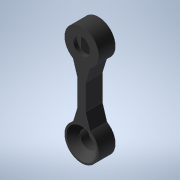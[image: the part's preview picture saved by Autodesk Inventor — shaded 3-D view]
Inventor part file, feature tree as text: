
AUTODESK INVENTOR PART (.ipt)
format: ipt  version: 2022 (Build 260153000, 153)  size: 199,168 bytes
history: native  units: in
note: dims shown in document units (in); Inventor stores cm internally (conversion verified against a paired STEP export)
features: extrude x8, sketch x8, chamfer x1
ambient origin geometry x8: Origin, YZ Plane, XZ Plane, XY Plane, X Axis, Y Axis, Z Axis, Center Point
bodies: Solid1 (feature_tree)
feature tree (17):
  extrude  "Extrusion1"  Depth=0.7874in
  extrude  "Extrusion2"  Depth=3.937in
  extrude  "Extrusion3"  Depth=1.5748in
  extrude  "Extrusion4"  Depth=0.7874in TaperAngle=0.0deg
  extrude  "Extrusion5"  Depth=0.1969in TaperAngle=0.0deg
  extrude  "Extrusion6"  Depth=0.6693in
  extrude  "Extrusion7"  Depth=0.5906in
  chamfer  "Chamfer1"  Distance=0.5906in
  extrude  "Extrusion8"  Depth=0.185in
  sketch  "Sketch1"  dims[d0=0.7874in d1=2.3622in]
  sketch  "Sketch2"  dims[d2=0.3937in d3=3.937in]
  sketch  "Sketch3"  dims[d4=2.3622in d5=1.5748in]
  sketch  "Sketch4"  dims[d6=1.5748in d7=0.7874in d8=0.0in]
  sketch  "Sketch5"  dims[d9=0.7874in d10=0.1969in d11=0.0in]
  sketch  "Sketch6"  dims[d12=0.2362in d13=0.6693in]
  sketch  "Sketch7"  dims[d14=0.2362in d15=0.2362in d16=0.5906in d17=0.0in]
  sketch  "Sketch8"  dims[d18=0.4724in d19=0.185in d20=0.185in d21=0.4528in d22=0.0in d23=0.0906in d24=0.0906in d25=0.0591in d26=0.0591in d27=1.9281in d28=0.0in d29=0.0787in d30=0.0in d31=0.1181in d32=0.1181in d33=0.1181in d34=0.4213in d35=0.0in d36=0.315in d37=0.0787in d38=45.0deg d39=1.5162in d40=0.0in]
